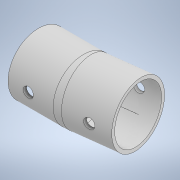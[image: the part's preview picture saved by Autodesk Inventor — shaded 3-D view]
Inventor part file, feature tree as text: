
AUTODESK INVENTOR PART (.ipt)
format: ipt  version: 2022 (Build 260153000, 153)  size: 240,640 bytes
history: native  units: mm
features: sketch x4, extrude x2, sweep x1
ambient origin geometry x8: Origin, YZ Plane, XZ Plane, XY Plane, X Axis, Y Axis, Z Axis, Center Point
bodies: Body1 (feature_tree)
feature tree (7):
  sweep  "Sweep1"
  extrude  "Extrusion8"  Depth=30.194196mm
  extrude  "Extrusion9"  Depth=10.0mm
  sketch  "Sketch5"  dims[d31=34.456mm d122=14.0mm]
  sketch  "Sketch6"  dims[d123=14.0mm d124=30.194196mm]
  sketch  "Sketch7"  dims[d125=10.0mm d126=16.0mm]
  sketch  "Sketch8"  dims[d127=18.0mm d128=0.0mm d129=0.0mm d130=6.0mm d131=3.0mm d132=25.0mm d133=0.0mm d134=6.0mm d135=3.0mm d136=25.0mm d137=0.0mm d138=0.01mm d139=0.01mm]
